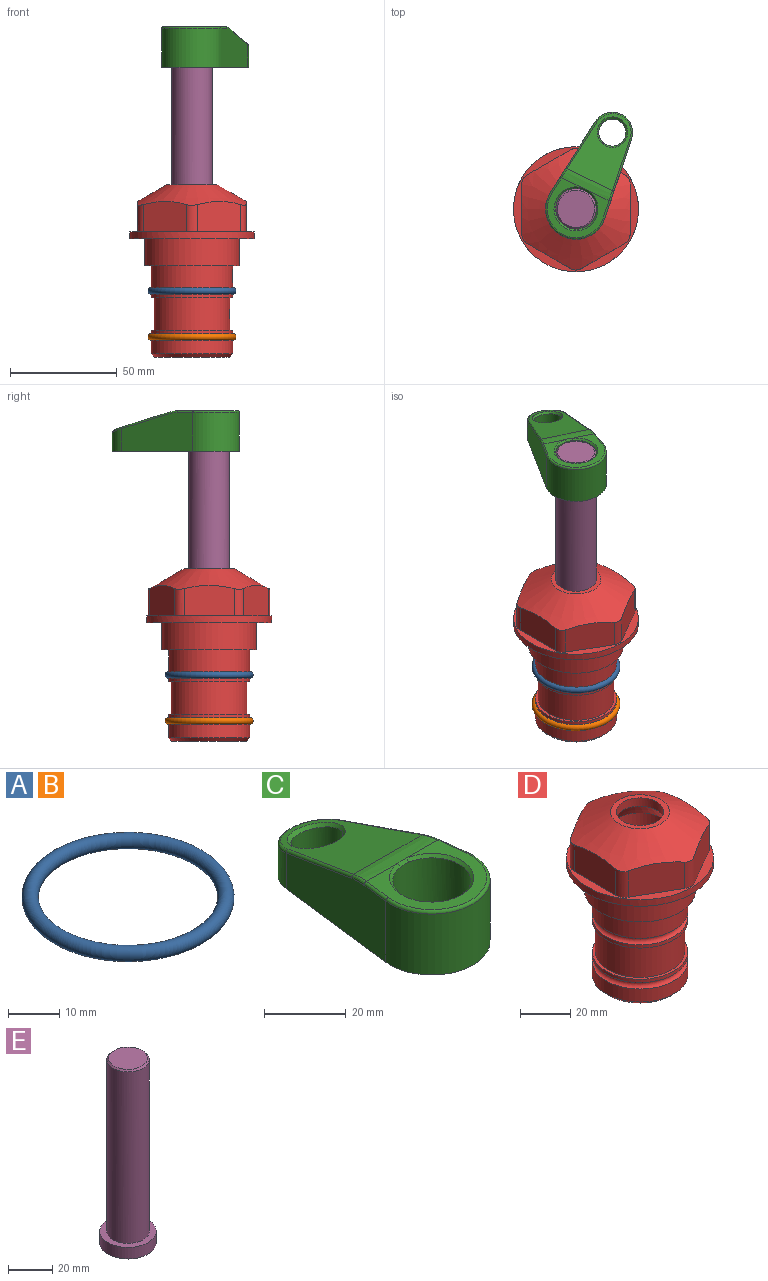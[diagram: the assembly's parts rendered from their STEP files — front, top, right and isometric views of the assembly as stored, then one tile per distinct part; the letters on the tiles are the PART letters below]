
ASSEMBLY  parts=5 mates=4
PART A: 1 faces, bbox 44.7x44.7x3.2 mm
  f0: torus R=19.05mm, axis (0,0,1), area 1193.9mm2
PART B: same geometry as A
PART C: 31 faces, bbox 31.7x65.5x19.8 mm
  f0: plane 39.12x18.26mm, normal (0.99,0.12,0), area 612.2mm2, adj f1,f4,f7,f11,f13,f15
  f1: cylinder r=9.53mm len=18.91mm, axis (0,0,-1), area 296.1mm2, adj f0,f2,f7,f17
  f2: plane 39.12x18.26mm, normal (-0.99,0.12,0), area 612.2mm2, adj f1,f4,f7,f12,f14,f16
  f3: cylinder r=6.35mm len=12.7mm, axis (0,0,-1), area 362.4mm2, adj f7,f18
  f4: cylinder r=14.29mm len=28.58mm, axis (0,0,-1), area 882.2mm2, adj f0,f2,f7,f10
  f5: cylinder r=9.53mm len=19.05mm, axis (0,0,-1), area 1092.6mm2, adj f7,f19,f20
  f6: plane 26.99x23.69mm, normal (0,0,1), area 216.2mm2, adj f9,f10,f11,f12,f19
  f7: plane 63.5x28.58mm, normal (0,0,-1), area 661.8mm2, adj f0,f1,f2,f3,f4,f5,f22,f23
  f8: plane 33.52x23.6mm, normal (0,0.26,0.97), area 486mm2, adj f9,f15,f16,f17,f18
  f9: cylinder r=19.05mm len=24.72mm, axis (1,0,0), area 120.4mm2, adj f6,f8,f13,f14,f20
  f10: torus R=13.49mm, axis (0,0,1), area 59mm2, adj f4,f6,f11,f12
  f11: cylinder r=0.79mm len=8.67mm, axis (0.12,-0.99,0), area 10.8mm2, adj f0,f6,f10,f13
  f12: cylinder r=0.79mm len=8.67mm, axis (0.12,0.99,0), area 10.8mm2, adj f2,f6,f10,f14
  f13: bspline ~4.95x1.42mm, area 6.1mm2, adj f0,f9,f11,f15
  f14: bspline ~4.95x1.42mm, area 6.1mm2, adj f2,f9,f12,f16
  f15: cylinder r=0.79mm len=25.95mm, axis (0.12,-0.96,0.26), area 32.9mm2, adj f0,f8,f13,f17
  f16: cylinder r=0.79mm len=25.95mm, axis (0.12,0.96,-0.26), area 32.9mm2, adj f2,f8,f14,f17
  f17: bspline ~18.91x8.38mm, area 30mm2, adj f1,f8,f15,f16
  f18: bspline ~14.29x14.29mm, area 48.3mm2, adj f3,f8
  f19: cone r=9.53mm half-angle=45deg, axis (0,0,1), area 66.5mm2, adj f5,f6,f20
  f20: bspline ~3.22x0.96mm, area 3.5mm2, adj f5,f9,f19
  f21: plane 2.75x2.72mm, normal (0,0,-1), area 2.9mm2, adj f23,f25,f28
  f22: plane 23.05x15.88mm, normal (-0.99,-0.12,0), area 323.6mm2, adj f7,f25,f26,f27,f28,f29
  f23: plane 23.05x15.88mm, normal (0.99,-0.12,0), area 323.6mm2, adj f7,f21,f25,f27,f28,f30
  f24: cylinder r=9.53mm len=10.69mm, axis (0,0,-1), area 114.7mm2, adj f7,f27,f29,f30
  f25: cylinder r=12.7mm len=20.59mm, axis (0,0,-1), area 381.1mm2, adj f7,f21,f22,f23,f26,f28
  f26: plane 2.75x2.72mm, normal (0,0,-1), area 2.9mm2, adj f22,f25,f28
  f27: plane 19.72x18.37mm, normal (0,-0.26,-0.97), area 291.8mm2, adj f22,f23,f24,f28,f29,f30
  f28: cylinder r=15.88mm len=19.92mm, axis (1,0,0), area 54.8mm2, adj f21,f22,f23,f25,f26,f27
  f29: cylinder r=1.59mm len=11mm, axis (0,0,-1), area 34.7mm2, adj f7,f22,f24,f27
  f30: cylinder r=1.59mm len=11mm, axis (0,0,-1), area 34.7mm2, adj f7,f23,f24,f27
PART D: 36 faces, bbox 58.7x58.7x81 mm
  f0: cylinder r=17.78mm len=35.56mm, axis (0,0,1), area 1670.8mm2, adj f23,f24,f31
  f1: cylinder r=19.05mm len=38.1mm, axis (0,0,1), area 1191.9mm2, adj f26,f27,f30
  f2: plane 58.66x58.66mm, normal (0,0,-1), area 1150.6mm2, adj f3,f28
  f3: cylinder r=29.33mm len=58.66mm, axis (0,0,-1), area 585.1mm2, adj f2,f4
  f4: plane 58.66x58.66mm, normal (0,0,1), area 475.9mm2, adj f3,f5,f6,f7,f8,f9,f10,f11
  f5: plane 20.32x14.34mm, normal (-0.5,0.87,0), area 324.4mm2, adj f4,f15,f16,f17
  f6: plane 20.32x14.34mm, normal (0.5,0.87,0), area 324.4mm2, adj f4,f14,f15,f17
  f7: plane 23.48x14.34mm, normal (1,0,0), area 324.4mm2, adj f4,f13,f14,f17
  f8: plane 20.32x14.34mm, normal (0.5,-0.87,0), area 324.4mm2, adj f4,f12,f13,f17
  f9: plane 20.32x14.34mm, normal (-0.5,-0.87,0), area 324.4mm2, adj f4,f11,f12,f17
  f10: plane 23.48x14.34mm, normal (-1,0,0), area 324.4mm2, adj f4,f11,f16,f17
  f11: cylinder r=5.08mm len=12.85mm, axis (0,0,-1), area 67.2mm2, adj f4,f9,f10,f17
  f12: cylinder r=5.08mm len=12.85mm, axis (0,0,-1), area 67.2mm2, adj f4,f8,f9,f17
  f13: cylinder r=5.08mm len=12.85mm, axis (0,0,-1), area 67.2mm2, adj f4,f7,f8,f17
  f14: cylinder r=5.08mm len=12.85mm, axis (0,0,-1), area 67.2mm2, adj f4,f6,f7,f17
  f15: cylinder r=5.08mm len=12.85mm, axis (0,0,-1), area 67.2mm2, adj f4,f5,f6,f17
  f16: cylinder r=5.08mm len=12.85mm, axis (0,0,-1), area 67.2mm2, adj f4,f5,f10,f17
  f17: cone r=11.73mm half-angle=60deg, axis (0,0,-1), area 2071.8mm2, adj f5,f6,f7,f8,f9,f10,f11,f12
  f18: plane 23.46x23.46mm, normal (0,0,1), area 147.4mm2, adj f17,f35
  f19: plane 34.93x34.93mm, normal (0,0,-1), area 958mm2, adj f29
  f20: cylinder r=19.05mm len=38.1mm, axis (0,0,1), area 760.1mm2, adj f21,f29
  f21: torus R=19.05mm, axis (0,0,1), area 565.3mm2, adj f20,f22
  f22: cylinder r=19.05mm len=38.1mm, axis (0,0,1), area 190mm2, adj f21,f23
  f23: plane 38.1x38.1mm, normal (0,0,1), area 146.9mm2, adj f0,f22
  f24: plane 38.1x38.1mm, normal (0,0,-1), area 146.9mm2, adj f0,f25
  f25: cylinder r=19.05mm len=38.1mm, axis (0,0,1), area 190mm2, adj f24,f26
  f26: torus R=19.05mm, axis (0,0,1), area 565.3mm2, adj f1,f25
  f27: plane 44.45x44.45mm, normal (0,0,-1), area 411.7mm2, adj f1,f28
  f28: cylinder r=22.23mm len=44.45mm, axis (0,0,1), area 1773.5mm2, adj f2,f27
  f29: cone r=19.05mm half-angle=45deg, axis (0,0,1), area 257.5mm2, adj f19,f20
  f30: cylinder r=3.17mm len=6.75mm, axis (-1,0,0), area 128mm2, adj f1,f33
  f31: cylinder r=3.17mm len=6.35mm, axis (-1,0,0), area 102.5mm2, adj f0,f33
  f32: plane 25.4x25.4mm, normal (0,0,1), area 506.7mm2, adj f33
  f33: cylinder r=12.7mm len=66.42mm, axis (0,0,-1), area 5236.2mm2, adj f30,f31,f32,f34
  f34: cone r=9.53mm half-angle=30deg, axis (0,0,-1), area 443.4mm2, adj f33,f35
  f35: cylinder r=9.53mm len=19.05mm, axis (0,0,-1), area 240.9mm2, adj f18,f34
PART E: 6 faces, bbox 25.4x25.4x101.6 mm
  f0: plane 17.46x17.46mm, normal (0,0,1), area 239.5mm2, adj f5
  f1: plane 25.4x25.4mm, normal (0,0,-1), area 506.7mm2, adj f2
  f2: cylinder r=12.7mm len=25.4mm, axis (0,0,1), area 506.7mm2, adj f1,f3
  f3: plane 25.4x25.4mm, normal (0,0,1), area 221.7mm2, adj f2,f4
  f4: cylinder r=9.53mm len=94.46mm, axis (0,0,1), area 5653mm2, adj f3,f5
  f5: cone r=8.73mm half-angle=45deg, axis (0,0,-1), area 64.4mm2, adj f0,f4
PLACE A at identity
PLACE B t=(0,0,-21.59)mm
PLACE C rot(axis=(0,0,-1),25.4deg) t=(0,0,35.97)mm
PLACE D at identity fixed
PLACE E rot(axis=(0,0,-1),25.4deg) t=(0,0,35.17)mm
MATE fastened A.f0 <-> D.f0  axis (0,0,1) through (0,0,-24.51)mm
MATE cylindrical E.f2 <-> D.f0  axis (0,0,-1) through (0,0,-2.93)mm
MATE fastened C.f4 <-> E.f2  axis (0,0,1) through (0,0,98.67)mm
MATE fastened B.f0 <-> D.f0  axis (0,0,1) through (0,0,-46.1)mm
